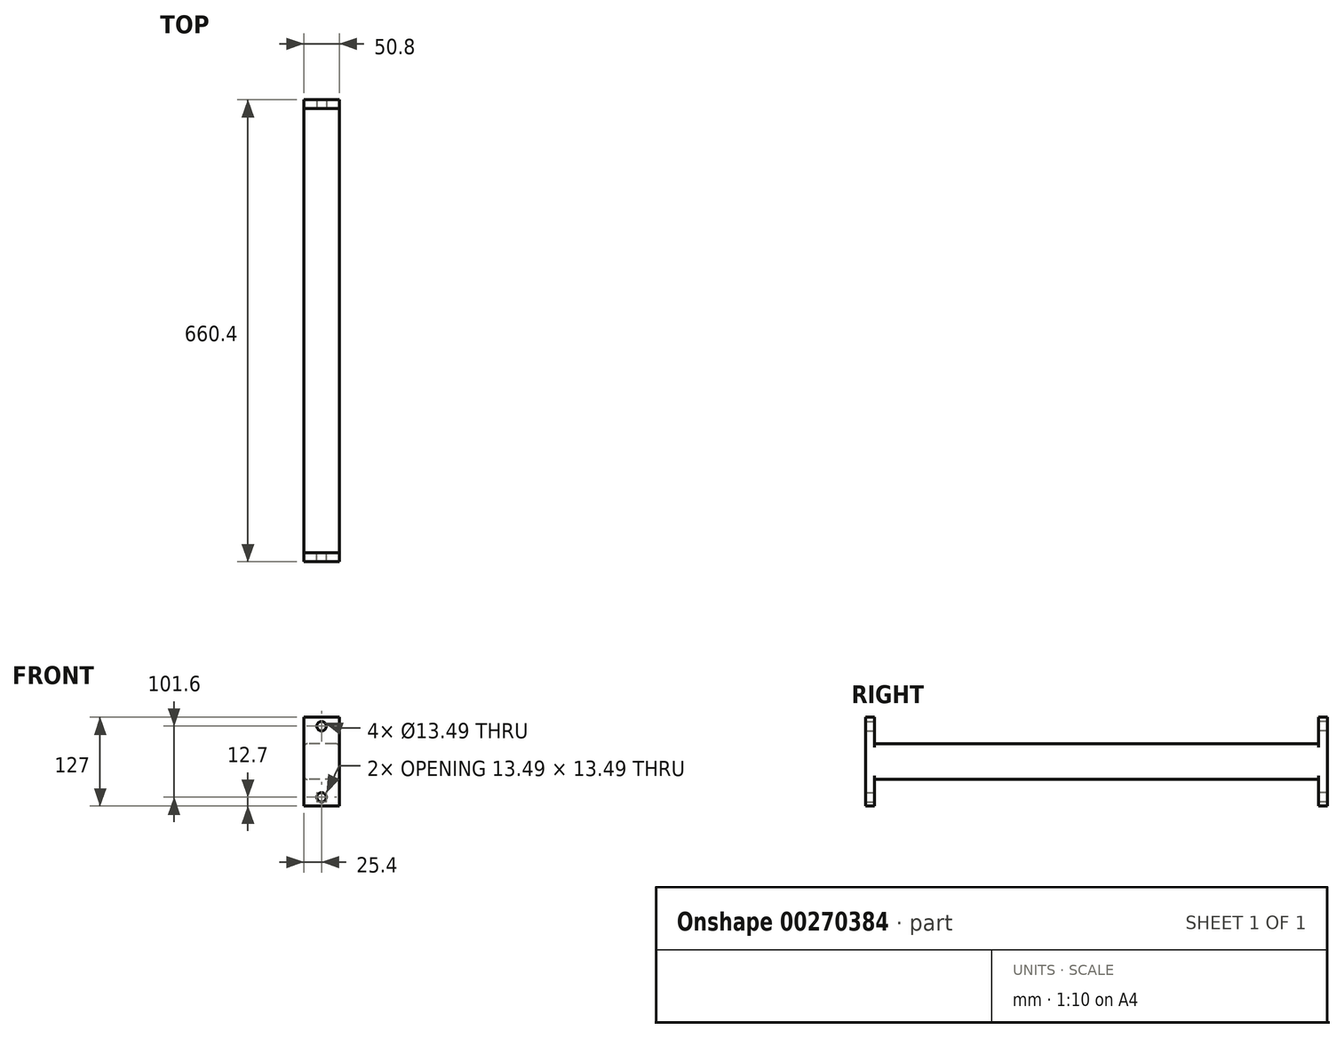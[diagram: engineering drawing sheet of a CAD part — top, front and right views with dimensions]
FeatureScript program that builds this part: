
annotation { "Feature Type Name" : "Feature", "Feature Type Description" : "" }
export const myFeature = defineFeature(function(context is Context, id is Id, definition is map)
    precondition{}
    {
        {
            var Q0;
            Q0=qCreatedBy(makeId("Front.planeOp"),FACE);
            var sketch = newSketch(context, id + "F0", { "sketchPlane" : qUnion([Q0])});
            skLineSegment(sketch, "E0.bottom", {"start": v(25.4, -25.4) * mm, "end": v(-25.4, -25.4) * mm});
            skLineSegment(sketch, "E0.top", {"start": v(25.4, 25.4) * mm, "end": v(-25.4, 25.4) * mm});
            skLineSegment(sketch, "E0.left", {"start": v(25.4, -25.4) * mm, "end": v(25.4, 25.4) * mm});
            skLineSegment(sketch, "E0.right", {"start": v(-25.4, -25.4) * mm, "end": v(-25.4, 25.4) * mm});
            skPoint(sketch, "E0.middle", {"position": v(0, 0) * mm});
            skSolve(sketch);
        }
        {
            var Q0;
            Q0=makeQuery(id+"F0.imprint","IMPRINT",FACE,{"disambiguationData":[TD([[makeQuery(id+"F0.imprint","IMPRINT",EDGE,{"derivedFrom":sQuery(id+"F0.wireOp",EDGE,"E0.bottom")}),-1.0]])]});
            extrude(context, id + "F1", {"entities" : qUnion([Q0]), "endBound" : BoundingType.SYMMETRIC, "depth" : 635 * mm});
        }
        {
            var Q0;
            Q0=makeQuery(id+"F1.opExtrude","CAP_FACE",FACE,{"disambiguationData":[OSD([sQuery(id+"F0.wireOp",EDGE,"E0.bottom"),sQuery(id+"F0.wireOp",EDGE,"E0.top"),sQuery(id+"F0.wireOp",EDGE,"E0.left"),sQuery(id+"F0.wireOp",EDGE,"E0.right")])],"isStart":false});
            var sketch = newSketch(context, id + "F2", { "sketchPlane" : qUnion([Q0])});
            skLineSegment(sketch, "E1.bottom", {"start": v(-25.4, 63.5) * mm, "end": v(25.4, 63.5) * mm});
            skLineSegment(sketch, "E1.top", {"start": v(-25.4, -63.5) * mm, "end": v(25.4, -63.5) * mm});
            skLineSegment(sketch, "E1.left", {"start": v(-25.4, 63.5) * mm, "end": v(-25.4, -63.5) * mm});
            skLineSegment(sketch, "E1.right", {"start": v(25.4, 63.5) * mm, "end": v(25.4, -63.5) * mm});
            skPoint(sketch, "E1.middle", {"position": v(0, 0) * mm});
            skPoint(sketch, "E2", {"position": v(0, 50.8) * mm});
            skPoint(sketch, "E3.MirrorP", {"position": v(0, -50.8) * mm});
            skSolve(sketch);
        }
        {
            var Q0;
            {var subQ0=sQuery(id+"F2.wireOp",EDGE,"E1.bottom");Q0=makeQuery(id+"F2.imprint","IMPRINT",FACE,{"disambiguationData":[TD([[makeQuery(id+"F2.imprint","IMPRINT",EDGE,{"derivedFrom":subQ0}),-1.0]])]});}
            var Q1;
            {var subQ1=makeQuery(id+"F1.opExtrude","CAP_EDGE",EDGE,{"disambiguationData":[OSD([sQuery(id+"F0.wireOp",EDGE,"E0.bottom")])],"isStart":false});Q1=makeQuery(id+"F2.imprint","IMPRINT",FACE,{"disambiguationData":[TD([[makeQuery(id+"F2.imprint","IMPRINT",EDGE,{"derivedFrom":subQ1}),-1.0]])]});}
            var Q2;
            {var subQ0=sQuery(id+"F2.wireOp",EDGE,"E1.top");Q2=makeQuery(id+"F2.imprint","IMPRINT",FACE,{"disambiguationData":[TD([[makeQuery(id+"F2.imprint","IMPRINT",EDGE,{"derivedFrom":subQ0}),1.0]])]});}
            extrude(context, id + "F3", {"entities" : qUnion([Q0, Q1, Q2]), "operationType" : NewBodyOperationType.ADD, "depth" : 12.7 * mm});
        }
        {
            var Q0;
            Q0=makeQuery(id+"F1.opExtrude","SWEPT_EDGE",EDGE,{"disambiguationData":[OSD([sQuery(id+"F0.wireOp",EDGE,"E0.top"),sQuery(id+"F0.wireOp",EDGE,"E0.left")])]});
            var Q1;
            Q1=makeQuery(id+"F1.opExtrude","SWEPT_EDGE",EDGE,{"disambiguationData":[OSD([sQuery(id+"F0.wireOp",EDGE,"E0.top"),sQuery(id+"F0.wireOp",EDGE,"E0.right")])]});
            var Q2;
            Q2=makeQuery(id+"F1.opExtrude","SWEPT_EDGE",EDGE,{"disambiguationData":[OSD([sQuery(id+"F0.wireOp",EDGE,"E0.bottom"),sQuery(id+"F0.wireOp",EDGE,"E0.right")])]});
            var Q3;
            Q3=makeQuery(id+"F1.opExtrude","SWEPT_EDGE",EDGE,{"disambiguationData":[OSD([sQuery(id+"F0.wireOp",EDGE,"E0.bottom"),sQuery(id+"F0.wireOp",EDGE,"E0.left")])]});
            fillet(context, id + "F4", {"entities" : qUnion([Q0, Q1, Q2, Q3]), "radius" : 5.08 * mm, "tangentPropagation" : true, "allowEdgeOverflow" : false});
        }
        {
            var Q0;
            Q0=sQuery(id+"F2.wireOp",VERTEX,"E2");
            var Q1;
            Q1=sQuery(id+"F2.wireOp",VERTEX,"E3.MirrorP");
            var Q2;
            Q2=makeQuery(id+"F1.opExtrude","SWEPT_BODY",BODY,{"disambiguationData":[OSD([sQuery(id+"F0.wireOp",EDGE,"E0.bottom"),sQuery(id+"F0.wireOp",EDGE,"E0.top"),sQuery(id+"F0.wireOp",EDGE,"E0.left"),sQuery(id+"F0.wireOp",EDGE,"E0.right")])]});
            hole(context, id + "F5", {"style" : HoleStyle.SIMPLE, "endStyle" : HoleEndStyle.THROUGH, "oppositeDirection" : true, "standardTappedOrClearance" : lookupTablePath({ "standard" : "ANSI", "fit" : "Normal (ASME)", "size" : "1/2", "type" : "Clearance" }), "standardBlindInLast" : lookupTablePath({ "fit" : "Free", "standard" : "ANSI", "size" : "1/2", "type" : "Clearance" }), "holeDiameter" : 13.5 * mm, "tappedDepth" : 12.7 * mm, "tapClearance" : 3, "startFromSketch" : true, "locations" : qUnion([Q0, Q1]), "scope" : qUnion([Q2])});
        }
        {
            var Q0;
            Q0=makeQuery(id+"F1.opExtrude","SWEPT_BODY",BODY,{"disambiguationData":[OSD([sQuery(id+"F0.wireOp",EDGE,"E0.bottom"),sQuery(id+"F0.wireOp",EDGE,"E0.top"),sQuery(id+"F0.wireOp",EDGE,"E0.left"),sQuery(id+"F0.wireOp",EDGE,"E0.right")])]});
            var Q1;
            Q1=qCreatedBy(makeId("Front.planeOp"),FACE);
            mirror(context, id + "F6", {"operationType" : NewBodyOperationType.ADD, "entities" : qUnion([Q0]), "mirrorPlane" : qUnion([Q1])});
        }
    });
